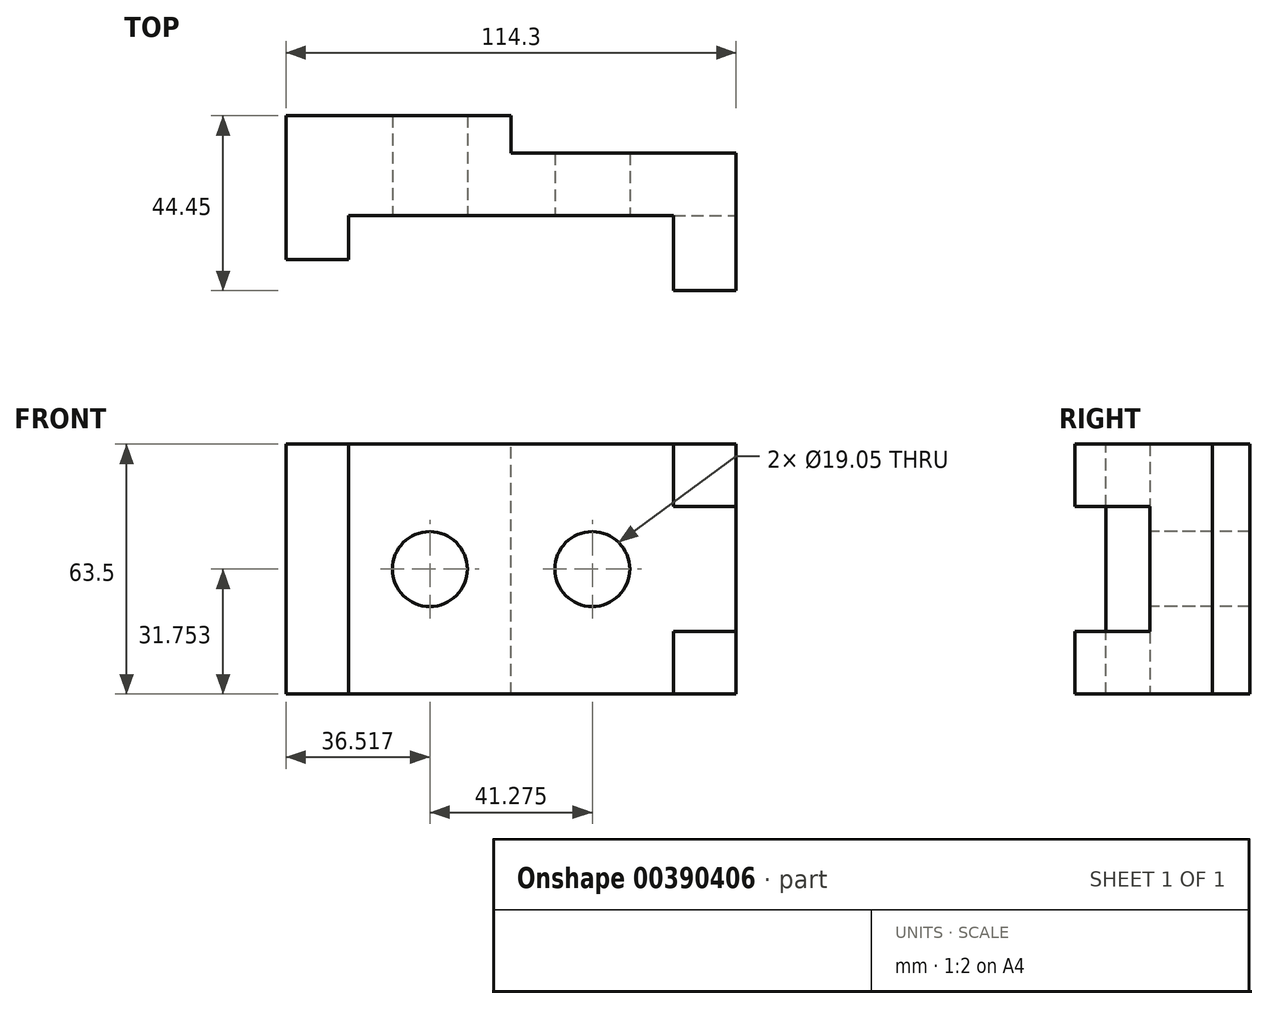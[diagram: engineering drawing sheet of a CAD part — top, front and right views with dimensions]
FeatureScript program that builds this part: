
annotation { "Feature Type Name" : "Feature", "Feature Type Description" : "" }
export const myFeature = defineFeature(function(context is Context, id is Id, definition is map)
    precondition{}
    {
        {
            var Q0;
            Q0=qCreatedBy(makeId("Front.planeOp"),FACE);
            var sketch = newSketch(context, id + "F0", { "sketchPlane" : qUnion([Q0])});
            skLineSegment(sketch, "E0", {"start": v(-44.87, 27.91) * mm, "end": v(-44.87, -35.59) * mm});
            skLineSegment(sketch, "E1", {"start": v(-44.87, -35.59) * mm, "end": v(69.43, -35.59) * mm});
            skLineSegment(sketch, "E2", {"start": v(69.43, -35.59) * mm, "end": v(69.43, 27.91) * mm});
            skLineSegment(sketch, "E3", {"start": v(69.43, 27.91) * mm, "end": v(-44.87, 27.91) * mm});
            skSolve(sketch);
        }
        {
            var Q0;
            Q0=makeQuery(id+"F0.imprint","IMPRINT",FACE,{"disambiguationData":[TD([[makeQuery(id+"F0.imprint","IMPRINT",EDGE,{"derivedFrom":sQuery(id+"F0.wireOp",EDGE,"E0")}),1.0]])]});
            extrude(context, id + "F1", {"entities" : qUnion([Q0]), "depth" : 25.4 * mm});
        }
        {
            var Q0;
            Q0=makeQuery(id+"F1.opExtrude","CAP_FACE",FACE,{"disambiguationData":[OSD([sQuery(id+"F0.wireOp",EDGE,"E0"),sQuery(id+"F0.wireOp",EDGE,"E1"),sQuery(id+"F0.wireOp",EDGE,"E2"),sQuery(id+"F0.wireOp",EDGE,"E3")])],"isStart":false});
            var sketch = newSketch(context, id + "F2", { "sketchPlane" : qUnion([Q0])});
            skLineSegment(sketch, "E4", {"start": v(-44.87, -35.59) * mm, "end": v(-29, -35.59) * mm});
            skLineSegment(sketch, "E5", {"start": v(-29, -35.59) * mm, "end": v(-29, 27.91) * mm});
            skLineSegment(sketch, "E6", {"start": v(-29, 27.91) * mm, "end": v(-44.87, 27.91) * mm});
            skLineSegment(sketch, "E7", {"start": v(-44.87, 27.91) * mm, "end": v(-44.87, -35.59) * mm});
            skSolve(sketch);
        }
        {
            var Q0;
            Q0=makeQuery(id+"F2.imprint","IMPRINT",FACE,{"disambiguationData":[TD([[makeQuery(id+"F2.imprint","IMPRINT",EDGE,{"derivedFrom":sQuery(id+"F2.wireOp",EDGE,"E4")}),1.0]])]});
            extrude(context, id + "F3", {"entities" : qUnion([Q0]), "operationType" : NewBodyOperationType.ADD, "depth" : 11.1 * mm});
        }
        {
            var Q0;
            Q0=makeQuery(id+"F1.opExtrude","CAP_FACE",FACE,{"disambiguationData":[OSD([sQuery(id+"F0.wireOp",EDGE,"E0"),sQuery(id+"F0.wireOp",EDGE,"E1"),sQuery(id+"F0.wireOp",EDGE,"E2"),sQuery(id+"F0.wireOp",EDGE,"E3")])],"isStart":false});
            var sketch = newSketch(context, id + "F4", { "sketchPlane" : qUnion([Q0])});
            skCircle(sketch, "E8", {"center": v(-8.35, -3.84) * mm, "radius": 9.53 * mm});
            skSolve(sketch);
        }
        {
            var Q0;
            Q0=makeQuery(id+"F4.imprint","IMPRINT",FACE,{"disambiguationData":[TD([[makeQuery(id+"F4.imprint","IMPRINT",EDGE,{"derivedFrom":sQuery(id+"F4.wireOp",EDGE,"E8")}),1.0]])]});
            extrude(context, id + "F5", {"entities" : qUnion([Q0]), "operationType" : NewBodyOperationType.REMOVE, "oppositeDirection" : true, "depth" : 25.4 * mm});
        }
        {
            var Q0;
            Q0=makeQuery(id+"F1.opExtrude","CAP_FACE",FACE,{"disambiguationData":[OSD([sQuery(id+"F0.wireOp",EDGE,"E0"),sQuery(id+"F0.wireOp",EDGE,"E1"),sQuery(id+"F0.wireOp",EDGE,"E2"),sQuery(id+"F0.wireOp",EDGE,"E3")])],"isStart":false});
            var sketch = newSketch(context, id + "F6", { "sketchPlane" : qUnion([Q0])});
            skCircle(sketch, "E9", {"center": v(32.92, -3.84) * mm, "radius": 9.53 * mm});
            skSolve(sketch);
        }
        {
            var Q0;
            Q0=makeQuery(id+"F6.imprint","IMPRINT",FACE,{"disambiguationData":[TD([[makeQuery(id+"F6.imprint","IMPRINT",EDGE,{"derivedFrom":sQuery(id+"F6.wireOp",EDGE,"E9")}),1.0]])]});
            extrude(context, id + "F7", {"entities" : qUnion([Q0]), "operationType" : NewBodyOperationType.REMOVE, "oppositeDirection" : true, "depth" : 25.4 * mm});
        }
        {
            var Q0;
            Q0=makeQuery(id+"F1.opExtrude","CAP_FACE",FACE,{"disambiguationData":[OSD([sQuery(id+"F0.wireOp",EDGE,"E0"),sQuery(id+"F0.wireOp",EDGE,"E1"),sQuery(id+"F0.wireOp",EDGE,"E2"),sQuery(id+"F0.wireOp",EDGE,"E3")])],"isStart":false});
            var sketch = newSketch(context, id + "F8", { "sketchPlane" : qUnion([Q0])});
            skLineSegment(sketch, "E10", {"start": v(69.43, 27.91) * mm, "end": v(53.56, 27.91) * mm});
            skLineSegment(sketch, "E11", {"start": v(53.56, 27.91) * mm, "end": v(53.56, -35.59) * mm});
            skLineSegment(sketch, "E12", {"start": v(53.56, -35.59) * mm, "end": v(69.43, -35.59) * mm});
            skLineSegment(sketch, "E13", {"start": v(69.43, -35.59) * mm, "end": v(69.43, 27.91) * mm});
            skSolve(sketch);
        }
        {
            var Q0;
            Q0=makeQuery(id+"F8.imprint","IMPRINT",FACE,{"disambiguationData":[TD([[makeQuery(id+"F8.imprint","IMPRINT",EDGE,{"derivedFrom":sQuery(id+"F8.wireOp",EDGE,"E10")}),1.0]])]});
            extrude(context, id + "F9", {"entities" : qUnion([Q0]), "operationType" : NewBodyOperationType.ADD, "depth" : 19.05 * mm});
        }
        {
            var Q0;
            Q0=makeQuery(id+"F9.opExtrude","CAP_FACE",FACE,{"disambiguationData":[OSD([sQuery(id+"F8.wireOp",EDGE,"E10"),sQuery(id+"F8.wireOp",EDGE,"E11"),sQuery(id+"F8.wireOp",EDGE,"E12"),sQuery(id+"F8.wireOp",EDGE,"E13")])],"isStart":false});
            var sketch = newSketch(context, id + "F10", { "sketchPlane" : qUnion([Q0])});
            skLineSegment(sketch, "E14", {"start": v(53.56, -19.71) * mm, "end": v(69.43, -19.71) * mm});
            skLineSegment(sketch, "E15", {"start": v(69.43, -19.71) * mm, "end": v(69.43, 12.04) * mm});
            skLineSegment(sketch, "E16", {"start": v(69.43, 12.04) * mm, "end": v(53.56, 12.04) * mm});
            skLineSegment(sketch, "E17", {"start": v(53.56, 12.04) * mm, "end": v(53.56, -19.71) * mm});
            skSolve(sketch);
        }
        {
            var Q0;
            Q0=makeQuery(id+"F10.imprint","IMPRINT",FACE,{"disambiguationData":[TD([[makeQuery(id+"F10.imprint","IMPRINT",EDGE,{"derivedFrom":sQuery(id+"F10.wireOp",EDGE,"E14")}),1.0]])]});
            extrude(context, id + "F11", {"entities" : qUnion([Q0]), "operationType" : NewBodyOperationType.REMOVE, "oppositeDirection" : true, "depth" : 19.05 * mm});
        }
        {
            var Q0;
            Q0=makeQuery(id+"F1.opExtrude","CAP_FACE",FACE,{"disambiguationData":[OSD([sQuery(id+"F0.wireOp",EDGE,"E0"),sQuery(id+"F0.wireOp",EDGE,"E1"),sQuery(id+"F0.wireOp",EDGE,"E2"),sQuery(id+"F0.wireOp",EDGE,"E3")])],"isStart":true});
            var sketch = newSketch(context, id + "F12", { "sketchPlane" : qUnion([Q0])});
            skLineSegment(sketch, "E18", {"start": v(-69.43, -35.59) * mm, "end": v(-12.28, -35.59) * mm});
            skLineSegment(sketch, "E19", {"start": v(-12.28, -35.59) * mm, "end": v(-12.28, 27.91) * mm});
            skLineSegment(sketch, "E20", {"start": v(-12.28, 27.91) * mm, "end": v(-69.43, 27.91) * mm});
            skLineSegment(sketch, "E21", {"start": v(-69.43, 27.91) * mm, "end": v(-69.43, -35.59) * mm});
            skSolve(sketch);
        }
        {
            var Q0;
            Q0=makeQuery(id+"F12.imprint","IMPRINT",FACE,{"disambiguationData":[TD([[makeQuery(id+"F12.imprint","IMPRINT",EDGE,{"derivedFrom":sQuery(id+"F12.wireOp",EDGE,"E18")}),-1.0]])]});
            extrude(context, id + "F13", {"entities" : qUnion([Q0]), "operationType" : NewBodyOperationType.REMOVE, "oppositeDirection" : true, "depth" : 9.52 * mm});
        }
    });
